# Revit family: KOMPAQ 100 CITY
name_source: partatom
category: Modelos genéricos
revit_build: Autodesk Revit 2017 (Build: 20170118_1100(x64)
units: mm (PartAtom-declared; Revit-internal decimal feet)

## family parameters
Compartido = No
Corte con vacíos al cargar = No
Cota de conector redondo = Diámetro de uso
Puede alojar armadura = No
Punto de cálculo de habitación = No
Tipo de pieza = Normal

## types (1)
- KVDH100.10R
    Altura = 235 mm  [stored 0.770997 ft]
    Anchura exterior = 154 mm  [stored 0.505249 ft]
    Anchura interior = 100 mm  [stored 0.328084 ft]
    Clase de carga = D-400 Norma EN-1433
    Costo = 74.30€
    Costo registrable = 106.50€
    Descripción = Canal de drenaje lineal, modelo ULMA KompaqDrain®City KVFDH100, monolítico con rejilla integrada en un solo cuerpo y sin discontinuidades, anti-vandálico y resistente a la corrosión. Clase de carga D-400 para el paso de todo tipo de vehículos y con orificios de captación de 8 mm de anchura. Sección en forma de V optimizada y orificios con geometría MAX-FLOW®: efecto auto-limpiante a bajo caudal, incremento de capacidad a caudal máximo y apertura positiva para evitar atasco de suciedad, para zonas sin pendiente en el terreno. Superficie activa con elementos direccionadores de la lámina de agua hacia los orificios de captación. Sistema de machihembrado de alineación horizontal y vertical, y ranura perimetral reformada para facilitar instalación de junta de sellado envolvente en 360˚. El elemento de registro y la arqueta superior incluyen la rejilla de fundición FNHX100FTDM. Disponen de preformas laterales para salidas horizontales a cada lado y preformas laterales para conexiones en T, el L y en cruz.
    Fabricante = ULMA Architectural
    Ficha técnica = http://www.ulmaarchitectural.com
    Modelo = KVDH100.10R
    Modelo registrable = AKVDH100MF10R
    Pendiente = 0.00%
    Peso = 32.60 kg
    Peso registrable = 40.00 kg
    Sección hidráulica = 139.50 cm²
    URL = http://www.ulmaarchitectural.com
    Ø salida horizontal = 110 mm
    Ø salida vertical = 110 mm

note: [stored X ft] marks values corroborated as IEEE doubles in the binary element streams (Revit-internal decimal feet)
